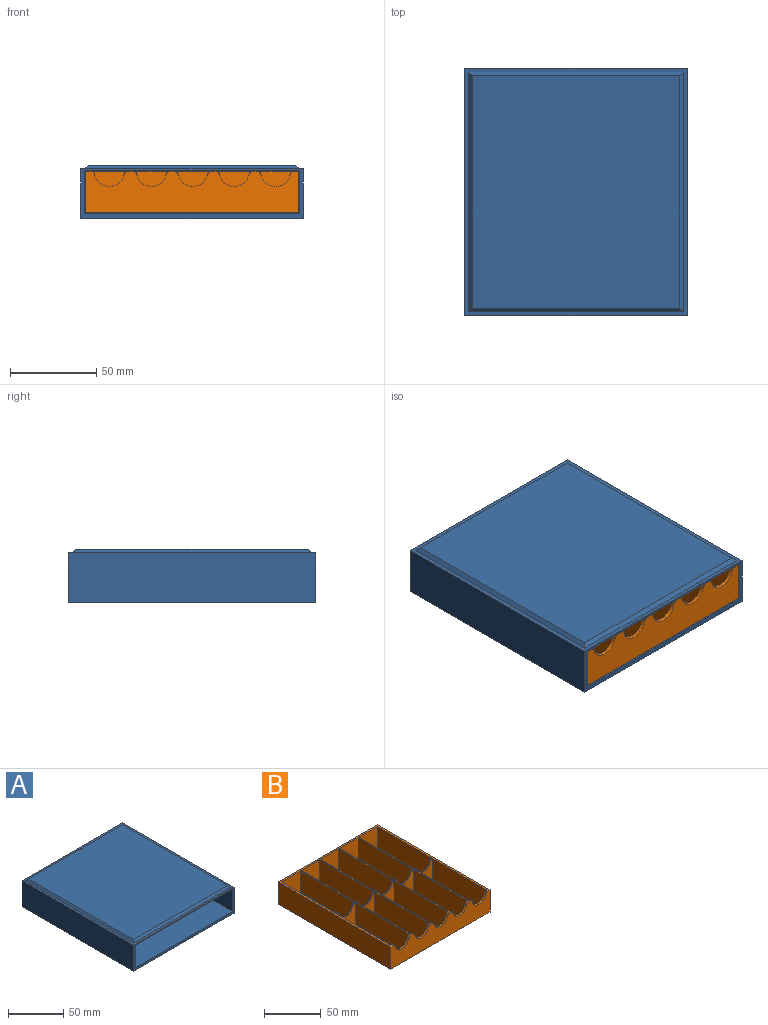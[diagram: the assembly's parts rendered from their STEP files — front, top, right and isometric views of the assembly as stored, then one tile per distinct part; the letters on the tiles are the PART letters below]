
ASSEMBLY  parts=2 mates=1
PART A: 26 faces, bbox 129x143.5x31 mm
  f0: plane 141.5x125mm, normal (0,0,-1), area 905mm2, adj f7,f13,f14,f15,f21,f22,f23,f24
  f1: plane 143.5x129mm, normal (0,0,1), area 1206mm2, adj f4,f5,f6,f7,f17,f18,f19,f20
  f2: plane 141.5x125mm, normal (0,0,1), area 17687.5mm2, adj f7,f13,f14,f15
  f3: plane 143.5x129mm, normal (0,0,-1), area 1074mm2, adj f4,f5,f6,f7,f9,f10,f11,f12
  f4: plane 143.5x29mm, normal (1,0,0), area 4161.5mm2, adj f1,f3,f5,f7
  f5: plane 129x29mm, normal (0,1,0), area 3741mm2, adj f1,f3,f4,f6
  f6: plane 143.5x29mm, normal (-1,0,0), area 4161.5mm2, adj f1,f3,f5,f7
  f7: plane 129x29mm, normal (0,-1,0), area 616mm2, adj f0,f1,f2,f3,f4,f6,f13,f14
  f8: plane 135.5x121mm, normal (0,0,-1), area 16395.5mm2, adj f9,f10,f11,f12
  f9: plane 139.5x2mm, normal (-0.71,0,-0.71), area 388.9mm2, adj f3,f8,f10,f11
  f10: plane 125x2mm, normal (0,0.71,-0.71), area 347.9mm2, adj f3,f8,f9,f12
  f11: plane 125x2mm, normal (0,-0.71,-0.71), area 347.9mm2, adj f3,f8,f9,f12
  f12: plane 139.5x2mm, normal (0.71,0,-0.71), area 388.9mm2, adj f3,f8,f10,f11
  f13: plane 141.5x25mm, normal (-1,0,0), area 3537.5mm2, adj f0,f2,f7,f15
  f14: plane 141.5x25mm, normal (1,0,0), area 3537.5mm2, adj f0,f2,f7,f15
  f15: plane 125x25mm, normal (0,-1,0), area 3125mm2, adj f0,f2,f13,f14
  f16: plane 135x120.5mm, normal (0,0,1), area 16267.5mm2, adj f17,f18,f19,f20
  f17: plane 139x2mm, normal (-0.71,0,0.71), area 387.5mm2, adj f1,f16,f18,f19
  f18: plane 124.5x2mm, normal (0,0.71,0.71), area 346.5mm2, adj f1,f16,f17,f20
  f19: plane 124.5x2mm, normal (0,-0.71,0.71), area 346.5mm2, adj f1,f16,f17,f20
  f20: plane 139x2mm, normal (0.71,0,0.71), area 387.5mm2, adj f1,f16,f18,f19
  f21: plane 137x2mm, normal (0.71,0,-0.71), area 381.8mm2, adj f0,f22,f24,f25
  f22: plane 122.5x2mm, normal (0,0.71,-0.71), area 340.8mm2, adj f0,f21,f23,f25
  f23: plane 137x2mm, normal (-0.71,0,-0.71), area 381.8mm2, adj f0,f22,f24,f25
  f24: plane 122.5x2mm, normal (0,-0.71,-0.71), area 340.8mm2, adj f0,f21,f23,f25
  f25: plane 133x118.5mm, normal (0,0,-1), area 15760.5mm2, adj f21,f22,f23,f24
PART B: 86 faces, bbox 124x141x24 mm
  f0: plane 141x124mm, normal (0,0,1), area 1391.1mm2, adj f1,f2,f3,f4,f5,f6,f7,f8
  f1: plane 68x23mm, normal (1,0,0), area 1564mm2, adj f0,f2,f44,f75
  f2: plane 23x23mm, normal (0,-1,0), area 529mm2, adj f0,f1,f3,f75
  f3: plane 68x23mm, normal (-1,0,0), area 1564mm2, adj f0,f2,f44,f75
  f4: plane 68x23mm, normal (1,0,0), area 1564mm2, adj f0,f5,f34,f84
  f5: plane 23x23mm, normal (0,-1,0), area 529mm2, adj f0,f4,f6,f84
  f6: plane 68x23mm, normal (-1,0,0), area 1564mm2, adj f0,f5,f34,f84
  f7: plane 23x23mm, normal (0,-1,0), area 407.5mm2, adj f0,f8,f35,f46,f73,f74,f83
  f8: plane 68x23mm, normal (-1,0,0), area 1564mm2, adj f0,f7,f9,f83
  f9: plane 23x23mm, normal (0,1,0), area 407.5mm2, adj f0,f8,f35,f45,f63,f64,f83
  f10: plane 68x23mm, normal (1,0,0), area 1564mm2, adj f0,f11,f36,f82
  f11: plane 23x23mm, normal (0,-1,0), area 529mm2, adj f0,f10,f12,f82
  f12: plane 68x23mm, normal (-1,0,0), area 1564mm2, adj f0,f11,f36,f82
  f13: plane 23x23mm, normal (0,1,0), area 407.5mm2, adj f0,f14,f37,f47,f61,f62,f81
  f14: plane 68x23mm, normal (1,0,0), area 1564mm2, adj f0,f13,f15,f81
  f15: plane 23x23mm, normal (0,-1,0), area 407.5mm2, adj f0,f14,f37,f48,f71,f72,f81
  f16: plane 24x23mm, normal (0,1,0), area 430.5mm2, adj f0,f17,f38,f54,f65,f66,f80
  f17: plane 68x23mm, normal (1,0,0), area 1564mm2, adj f0,f16,f18,f80
  f18: plane 24x23mm, normal (0,-1,0), area 552mm2, adj f0,f17,f38,f80
  f19: plane 24x23mm, normal (0,-1,0), area 430.5mm2, adj f0,f20,f39,f54,f65,f66,f79
  f20: plane 68x23mm, normal (-1,0,0), area 1564mm2, adj f0,f19,f21,f79
  f21: plane 24x23mm, normal (0,1,0), area 430.5mm2, adj f0,f20,f39,f53,f55,f56,f79
  f22: plane 141x24mm, normal (-1,0,0), area 3384mm2, adj f0,f23,f40,f85
  f23: plane 124x24mm, normal (0,-1,0), area 2368.4mm2, adj f0,f22,f24,f45,f47,f49,f51,f53
  f24: plane 141x24mm, normal (1,0,0), area 3384mm2, adj f0,f23,f40,f85
  f25: plane 23x23mm, normal (0,1,0), area 407.5mm2, adj f0,f26,f41,f49,f59,f60,f78
  f26: plane 68x23mm, normal (1,0,0), area 1564mm2, adj f0,f25,f27,f78
  f27: plane 23x23mm, normal (0,-1,0), area 407.5mm2, adj f0,f26,f41,f50,f69,f70,f78
  f28: plane 23x23mm, normal (0,1,0), area 407.5mm2, adj f0,f29,f42,f51,f57,f58,f77
  f29: plane 68x23mm, normal (1,0,0), area 1564mm2, adj f0,f28,f30,f77
  f30: plane 23x23mm, normal (0,-1,0), area 407.5mm2, adj f0,f29,f42,f52,f67,f68,f77
  f31: plane 68x23mm, normal (-1,0,0), area 1564mm2, adj f0,f32,f43,f76
  f32: plane 23x23mm, normal (0,1,0), area 407.5mm2, adj f0,f31,f33,f48,f71,f72,f76
  f33: plane 68x23mm, normal (1,0,0), area 1564mm2, adj f0,f32,f43,f76
  f34: plane 23x23mm, normal (0,1,0), area 407.5mm2, adj f0,f4,f6,f50,f69,f70,f84
  f35: plane 68x23mm, normal (1,0,0), area 1564mm2, adj f0,f7,f9,f83
  f36: plane 23x23mm, normal (0,1,0), area 407.5mm2, adj f0,f10,f12,f46,f73,f74,f82
  f37: plane 68x23mm, normal (-1,0,0), area 1564mm2, adj f0,f13,f15,f81
  f38: plane 68x23mm, normal (-1,0,0), area 1564mm2, adj f0,f16,f18,f80
  f39: plane 68x23mm, normal (1,0,0), area 1564mm2, adj f0,f19,f21,f79
  f40: plane 124x24mm, normal (0,1,0), area 2976mm2, adj f0,f22,f24,f85
  f41: plane 68x23mm, normal (-1,0,0), area 1564mm2, adj f0,f25,f27,f78
  f42: plane 68x23mm, normal (-1,0,0), area 1564mm2, adj f0,f28,f30,f77
  f43: plane 23x23mm, normal (0,-1,0), area 529mm2, adj f0,f31,f33,f76
  f44: plane 23x23mm, normal (0,1,0), area 407.5mm2, adj f0,f1,f3,f52,f67,f68,f75
  f45: cylinder r=8.75mm len=17.19mm, axis (0,-1,0), area 48.4mm2, adj f9,f23,f63,f64
  f46: cylinder r=8.75mm len=17.19mm, axis (0,-1,0), area 24.2mm2, adj f7,f36,f73,f74
  f47: cylinder r=8.75mm len=17.19mm, axis (0,-1,0), area 48.4mm2, adj f13,f23,f61,f62
  f48: cylinder r=8.75mm len=17.19mm, axis (0,-1,0), area 24.2mm2, adj f15,f32,f71,f72
  f49: cylinder r=8.75mm len=17.19mm, axis (0,-1,0), area 48.4mm2, adj f23,f25,f59,f60
  f50: cylinder r=8.75mm len=17.19mm, axis (0,-1,0), area 24.2mm2, adj f27,f34,f69,f70
  f51: cylinder r=8.75mm len=17.19mm, axis (0,-1,0), area 48.4mm2, adj f23,f28,f57,f58
  f52: cylinder r=8.75mm len=17.19mm, axis (0,-1,0), area 24.2mm2, adj f30,f44,f67,f68
  f53: cylinder r=8.75mm len=17.19mm, axis (0,-1,0), area 48.4mm2, adj f21,f23,f55,f56
  f54: cylinder r=8.75mm len=17.19mm, axis (0,-1,0), area 24.2mm2, adj f16,f19,f65,f66
  f55: cylinder r=2mm len=2mm, axis (0,-1,0), area 5.5mm2, adj f0,f21,f23,f53
  f56: cylinder r=2mm len=2mm, axis (0,-1,0), area 5.5mm2, adj f0,f21,f23,f53
  f57: cylinder r=2mm len=2mm, axis (0,-1,0), area 5.5mm2, adj f0,f23,f28,f51
  f58: cylinder r=2mm len=2mm, axis (0,-1,0), area 5.5mm2, adj f0,f23,f28,f51
  f59: cylinder r=2mm len=2mm, axis (0,-1,0), area 5.5mm2, adj f0,f23,f25,f49
  f60: cylinder r=2mm len=2mm, axis (0,-1,0), area 5.5mm2, adj f0,f23,f25,f49
  f61: cylinder r=2mm len=2mm, axis (0,-1,0), area 5.5mm2, adj f0,f13,f23,f47
  f62: cylinder r=2mm len=2mm, axis (0,-1,0), area 5.5mm2, adj f0,f13,f23,f47
  f63: cylinder r=2mm len=2mm, axis (0,-1,0), area 5.5mm2, adj f0,f9,f23,f45
  f64: cylinder r=2mm len=2mm, axis (0,-1,0), area 5.5mm2, adj f0,f9,f23,f45
  f65: cylinder r=2mm len=1.97mm, axis (0,-1,0), area 2.8mm2, adj f0,f16,f19,f54
  f66: cylinder r=2mm len=1.97mm, axis (0,-1,0), area 2.8mm2, adj f0,f16,f19,f54
  f67: cylinder r=2mm len=1.97mm, axis (0,-1,0), area 2.8mm2, adj f0,f30,f44,f52
  f68: cylinder r=2mm len=1.97mm, axis (0,-1,0), area 2.8mm2, adj f0,f30,f44,f52
  f69: cylinder r=2mm len=1.97mm, axis (0,-1,0), area 2.8mm2, adj f0,f27,f34,f50
  f70: cylinder r=2mm len=1.97mm, axis (0,-1,0), area 2.8mm2, adj f0,f27,f34,f50
  f71: cylinder r=2mm len=1.97mm, axis (0,-1,0), area 2.8mm2, adj f0,f15,f32,f48
  f72: cylinder r=2mm len=1.97mm, axis (0,-1,0), area 2.8mm2, adj f0,f15,f32,f48
  f73: cylinder r=2mm len=1.97mm, axis (0,-1,0), area 2.8mm2, adj f0,f7,f36,f46
  f74: cylinder r=2mm len=1.97mm, axis (0,-1,0), area 2.8mm2, adj f0,f7,f36,f46
  f75: plane 68x23mm, normal (0,0,1), area 1564mm2, adj f1,f2,f3,f44
  f76: plane 68x23mm, normal (0,0,1), area 1564mm2, adj f31,f32,f33,f43
  f77: plane 68x23mm, normal (0,0,1), area 1564mm2, adj f28,f29,f30,f42
  f78: plane 68x23mm, normal (0,0,1), area 1564mm2, adj f25,f26,f27,f41
  f79: plane 68x24mm, normal (0,0,1), area 1632mm2, adj f19,f20,f21,f39
  f80: plane 68x24mm, normal (0,0,1), area 1632mm2, adj f16,f17,f18,f38
  f81: plane 68x23mm, normal (0,0,1), area 1564mm2, adj f13,f14,f15,f37
  f82: plane 68x23mm, normal (0,0,1), area 1564mm2, adj f10,f11,f12,f36
  f83: plane 68x23mm, normal (0,0,1), area 1564mm2, adj f7,f8,f9,f35
  f84: plane 68x23mm, normal (0,0,1), area 1564mm2, adj f4,f5,f6,f34
  f85: plane 141x124mm, normal (0,0,-1), area 17484mm2, adj f22,f23,f24,f40
PLACE A at identity fixed
PLACE B t=(0,-1,3.5)mm
MATE slider A.f15 <-> B.f40  axis (0,-1,0) through (0,69.75,15.5)mm
